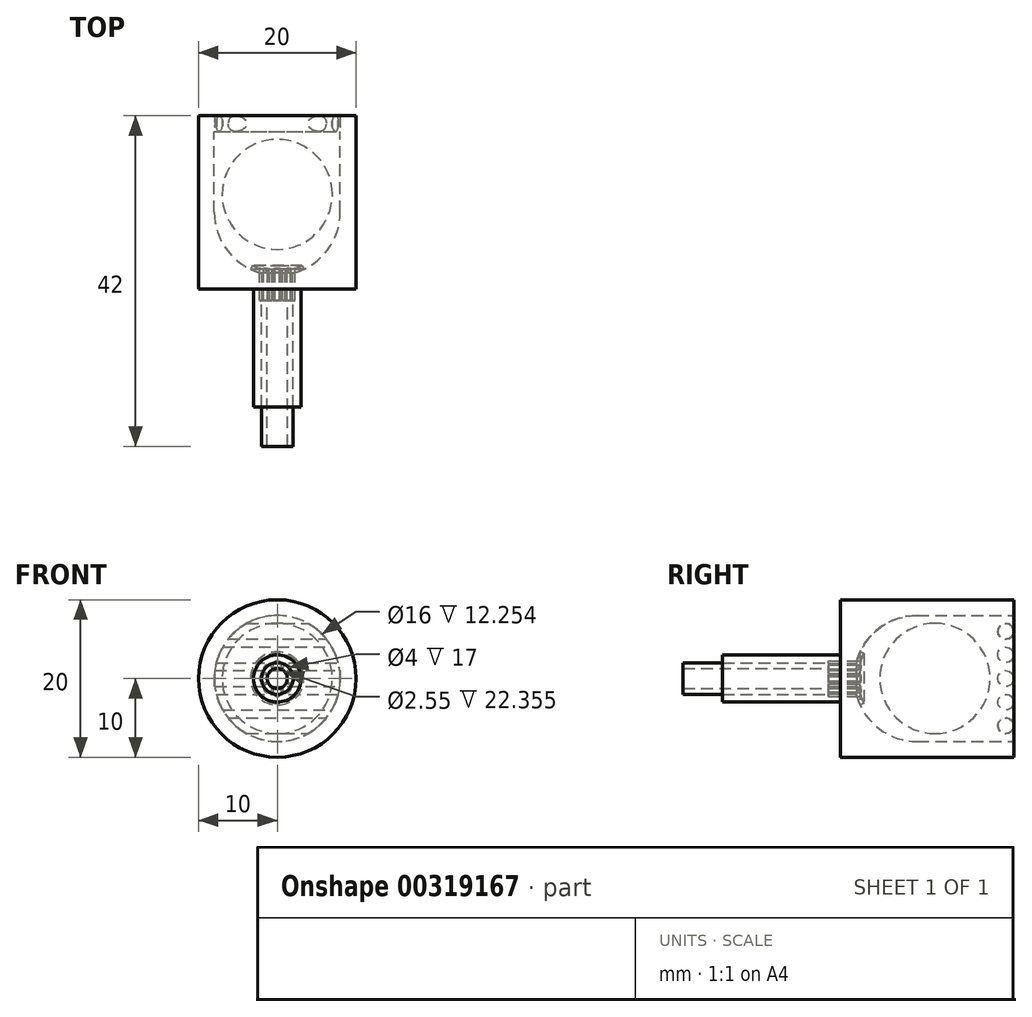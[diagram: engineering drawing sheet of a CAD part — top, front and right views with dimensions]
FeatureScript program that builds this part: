
annotation { "Feature Type Name" : "Feature", "Feature Type Description" : "" }
export const myFeature = defineFeature(function(context is Context, id is Id, definition is map)
    precondition{}
    {
        {
            var Q0;
            Q0=qCreatedBy(makeId("Right.planeOp"),FACE);
            var sketch = newSketch(context, id + "F0", { "sketchPlane" : qUnion([Q0])});
            skLineSegment(sketch, "E0", {"start": v(-37, 3) * mm, "end": v(-22, 3) * mm});
            skLineSegment(sketch, "E1", {"start": v(-22, 3) * mm, "end": v(-22, 2) * mm});
            skLineSegment(sketch, "E2", {"start": v(-22, 2) * mm, "end": v(-37, 2) * mm});
            skLineSegment(sketch, "E3", {"start": v(-37, 2) * mm, "end": v(-37, 3) * mm});
            skLineSegment(sketch, "E4", {"start": v(-22, 3) * mm, "end": v(-22, 10) * mm});
            skLineSegment(sketch, "E5", {"start": v(-22, 10) * mm, "end": v(0, 10) * mm});
            skLineSegment(sketch, "E6", {"start": v(0, 10) * mm, "end": v(0, 8) * mm});
            skLineSegment(sketch, "E7", {"start": v(0, 8) * mm, "end": v(-20, 8) * mm});
            skLineSegment(sketch, "E8", {"start": v(-20, 8) * mm, "end": v(-20, 2) * mm});
            skLineSegment(sketch, "E9", {"start": v(-20, 2) * mm, "end": v(-22, 2) * mm});
            skLineSegment(sketch, "E10", {"start": v(0, 0) * mm, "end": v(-46.36, 0) * mm, "construction": true});
            skCircle(sketch, "E11", {"center": v(-10, 0) * mm, "radius": 7 * mm});
            skCircle(sketch, "E12", {"center": v(-12.25, 0) * mm, "radius": 8 * mm});
            skLineSegment(sketch, "E13", {"start": v(-10, 7) * mm, "end": v(-10, -7) * mm});
            skLineSegment(sketch, "E14", {"start": v(-37, 2) * mm, "end": v(-42, 2) * mm});
            skLineSegment(sketch, "E15", {"start": v(-42, 2) * mm, "end": v(-42, 1.28) * mm});
            skLineSegment(sketch, "E16", {"start": v(-42, 1.28) * mm, "end": v(-18.5, 1.28) * mm});
            skLineSegment(sketch, "E17", {"start": v(-18.5, 1.28) * mm, "end": v(-18.5, 5) * mm});
            skCircle(sketch, "E18", {"center": v(-12.25, 0) * mm, "radius": 7.5 * mm});
            skLineSegment(sketch, "E19", {"start": v(-12.25, 0) * mm, "end": v(-19.5, 3.38) * mm, "construction": true});
            skLineSegment(sketch, "E20", {"start": v(-19.5, 3.38) * mm, "end": v(-19.05, 3.17) * mm});
            skSolve(sketch);
        }
        {
            var Q0;
            Q0=sQuery(id+"F0.wireOp",EDGE,"E17");
            cPlane(context, id + "F1", {"entities" : qUnion([Q0]), "cplaneType" : CPlaneType.LINE_ANGLE, "offset" : 25 * mm, "angle" : 90 * degree, "width" : 150 * mm, "height" : 150 * mm});
        }
        {
            var Q0;
            Q0=qCreatedBy(id+"F1.planeOp",FACE);
            var sketch = newSketch(context, id + "F2", { "sketchPlane" : qUnion([Q0])});
            skLineSegment(sketch, "E21.0", {"start": v(0, 1.28) * mm, "end": v(0, 5) * mm});
            skCircle(sketch, "E22", {"center": v(0, 1.68) * mm, "radius": 0.55 * mm});
            skCircle(sketch, "E23.1.0", {"center": v(-1.2, 1.17) * mm, "radius": 0.55 * mm});
            skCircle(sketch, "E23.2.0", {"center": v(-1.7, -0.03) * mm, "radius": 0.55 * mm});
            skCircle(sketch, "E23.3.0", {"center": v(-1.2, -1.23) * mm, "radius": 0.55 * mm});
            skCircle(sketch, "E23.4.0", {"center": v(0.01, -1.72) * mm, "radius": 0.55 * mm});
            skPoint(sketch, "E23.center", {"position": v(0, -0.02) * mm});
            skCircle(sketch, "E24.1.5.0", {"center": v(1.21, -1.22) * mm, "radius": 0.55 * mm});
            skCircle(sketch, "E24.1.6.0", {"center": v(1.7, -0.02) * mm, "radius": 0.55 * mm});
            skCircle(sketch, "E24.1.7.0", {"center": v(1.2, 1.18) * mm, "radius": 0.55 * mm});
            skSolve(sketch);
        }
        {
            var Q0;
            Q0=sQuery(id+"F0.wireOp",EDGE,"E6");
            cPlane(context, id + "F3", {"entities" : qUnion([Q0]), "cplaneType" : CPlaneType.LINE_ANGLE, "offset" : 25 * mm, "angle" : 0 * degree, "width" : 150 * mm, "height" : 150 * mm});
        }
        {
            var Q0;
            Q0=qCreatedBy(id+"F3.planeOp",FACE);
            var sketch = newSketch(context, id + "F4", { "sketchPlane" : qUnion([Q0])});
            skLineSegment(sketch, "E25.0", {"start": v(22, 10) * mm, "end": v(0, 10) * mm});
            skLineSegment(sketch, "E26.MirrorCS", {"start": v(22, -10) * mm, "end": v(0, -10) * mm});
            skLineSegment(sketch, "E27", {"start": v(1, 10) * mm, "end": v(1, -10) * mm, "construction": true});
            skCircle(sketch, "E28", {"center": v(1, 9) * mm, "radius": 1 * mm});
            skCircle(sketch, "E29.0.1.0", {"center": v(1, 6) * mm, "radius": 1 * mm});
            skCircle(sketch, "E29.0.2.0", {"center": v(1, 3) * mm, "radius": 1 * mm});
            skCircle(sketch, "E29.0.3.0", {"center": v(1, 0) * mm, "radius": 1 * mm});
            skCircle(sketch, "E29.0.4.0", {"center": v(1, -3) * mm, "radius": 1 * mm});
            skCircle(sketch, "E29.0.5.0", {"center": v(1, -6) * mm, "radius": 1 * mm});
            skCircle(sketch, "E29.0.6.0", {"center": v(1, -9) * mm, "radius": 1 * mm});
            skLineSegment(sketch, "E29.direction1", {"start": v(1, 9) * mm, "end": v(26, 9) * mm, "construction": true});
            skLineSegment(sketch, "E29.direction2", {"start": v(1, 9) * mm, "end": v(1, 6) * mm, "construction": true});
            skSolve(sketch);
        }
        {
            var Q0;
            Q0=makeQuery(id+"F0.imprint","IMPRINT",FACE,{"disambiguationData":[TD([[makeQuery(id+"F0.imprint","IMPRINT",EDGE,{"derivedFrom":sQuery(id+"F0.wireOp",EDGE,"E0")}),-1.0]])]});
            var Q1;
            Q1=makeQuery(id+"F0.imprint","IMPRINT",FACE,{"disambiguationData":[TD([[makeQuery(id+"F0.imprint","IMPRINT",EDGE,{"derivedFrom":sQuery(id+"F0.wireOp",EDGE,"E1")}),1.0]])]});
            var Q2;
            {var subQ0=sQuery(id+"F0.wireOp",EDGE,"E8");Q2=makeQuery(id+"F0.imprint","IMPRINT",FACE,{"disambiguationData":[TD([[makeQuery(id+"F0.imprint","IMPRINT",EDGE,{"derivedFrom":subQ0}),1.0]])]});}
            var Q3;
            Q3=sQuery(id+"F0.wireOp",EDGE,"E10");
            revolve(context, id + "F5", {"entities" : qUnion([Q0, Q1, Q2]), "axis" : qUnion([Q3]), "revolveType" : RevolveType.FULL});
        }
        {
            var Q0;
            {var subQ0=sQuery(id+"F0.wireOp",EDGE,"E13");Q0=makeQuery(id+"F0.imprint","IMPRINT",FACE,{"disambiguationData":[TD([[makeQuery(id+"F0.imprint","IMPRINT",EDGE,{"derivedFrom":subQ0}),-1.0]])]});}
            var Q1;
            Q1=sQuery(id+"F0.wireOp",EDGE,"E13");
            revolve(context, id + "F6", {"entities" : qUnion([Q0]), "axis" : qUnion([Q1]), "revolveType" : RevolveType.FULL});
        }
        {
            var Q0;
            {var subQ0=sQuery(id+"F0.wireOp",EDGE,"E20");Q0=makeQuery(id+"F0.imprint","IMPRINT",FACE,{"disambiguationData":[TD([[makeQuery(id+"F0.imprint","IMPRINT",EDGE,{"derivedFrom":subQ0}),-1.0]])]});}
            var Q1;
            Q1=makeQuery(id+"F0.imprint","IMPRINT",FACE,{"disambiguationData":[TD([[makeQuery(id+"F0.imprint","IMPRINT",EDGE,{"derivedFrom":sQuery(id+"F0.wireOp",EDGE,"E2")}),1.0]])]});
            var Q2;
            Q2=sQuery(id+"F0.wireOp",EDGE,"E10");
            revolve(context, id + "F7", {"entities" : qUnion([Q0, Q1]), "axis" : qUnion([Q2]), "revolveType" : RevolveType.FULL});
        }
        {
            var Q0;
            {var subQ0=sQuery(id+"F2.wireOp",EDGE,"E22");var subQ1=sQuery(id+"F2.wireOp",EDGE,"E21.0");var subQ2=makeQuery(id+"F2.imprint","INTERSECT",VERTEX,{"disambiguationData":[OD(0.0)],"derivedFrom":[subQ1,subQ0]});Q0=makeQuery(id+"F2.imprint","IMPRINT",FACE,{"disambiguationData":[TD([[makeQuery(id+"F2.imprint","IMPRINT",EDGE,{"disambiguationData":[TD([[subQ2,-1.0]])],"derivedFrom":subQ1}),1.0]])]});}
            var Q1;
            {var subQ0=sQuery(id+"F2.wireOp",EDGE,"E22");var subQ1=sQuery(id+"F2.wireOp",EDGE,"E21.0");var subQ2=makeQuery(id+"F2.imprint","INTERSECT",VERTEX,{"disambiguationData":[OD(0.0)],"derivedFrom":[subQ1,subQ0]});Q1=makeQuery(id+"F2.imprint","IMPRINT",FACE,{"disambiguationData":[TD([[makeQuery(id+"F2.imprint","IMPRINT",EDGE,{"disambiguationData":[TD([[subQ2,-1.0]])],"derivedFrom":subQ1}),-1.0]])]});}
            var Q2;
            Q2=makeQuery(id+"F2.imprint","IMPRINT",FACE,{"disambiguationData":[TD([[makeQuery(id+"F2.imprint","IMPRINT",EDGE,{"derivedFrom":sQuery(id+"F2.wireOp",EDGE,"E23.11.0")}),1.0]])]});
            var Q3;
            Q3=makeQuery(id+"F2.imprint","IMPRINT",FACE,{"disambiguationData":[TD([[makeQuery(id+"F2.imprint","IMPRINT",EDGE,{"derivedFrom":sQuery(id+"F2.wireOp",EDGE,"E23.10.0")}),1.0]])]});
            var Q4;
            Q4=makeQuery(id+"F2.imprint","IMPRINT",FACE,{"disambiguationData":[TD([[makeQuery(id+"F2.imprint","IMPRINT",EDGE,{"derivedFrom":sQuery(id+"F2.wireOp",EDGE,"E23.1.0")}),1.0]])]});
            var Q5;
            Q5=makeQuery(id+"F2.imprint","IMPRINT",FACE,{"disambiguationData":[TD([[makeQuery(id+"F2.imprint","IMPRINT",EDGE,{"derivedFrom":sQuery(id+"F2.wireOp",EDGE,"E23.2.0")}),1.0]])]});
            var Q6;
            Q6=makeQuery(id+"F2.imprint","IMPRINT",FACE,{"disambiguationData":[TD([[makeQuery(id+"F2.imprint","IMPRINT",EDGE,{"derivedFrom":sQuery(id+"F2.wireOp",EDGE,"E23.3.0")}),1.0]])]});
            var Q7;
            Q7=makeQuery(id+"F2.imprint","IMPRINT",FACE,{"disambiguationData":[TD([[makeQuery(id+"F2.imprint","IMPRINT",EDGE,{"derivedFrom":sQuery(id+"F2.wireOp",EDGE,"E23.4.0")}),1.0]])]});
            var Q8;
            Q8=makeQuery(id+"F2.imprint","IMPRINT",FACE,{"disambiguationData":[TD([[makeQuery(id+"F2.imprint","IMPRINT",EDGE,{"derivedFrom":sQuery(id+"F2.wireOp",EDGE,"E23.5.0")}),1.0]])]});
            var Q9;
            Q9=makeQuery(id+"F2.imprint","IMPRINT",FACE,{"disambiguationData":[TD([[makeQuery(id+"F2.imprint","IMPRINT",EDGE,{"derivedFrom":sQuery(id+"F2.wireOp",EDGE,"E23.6.0")}),1.0]])]});
            var Q10;
            Q10=makeQuery(id+"F2.imprint","IMPRINT",FACE,{"disambiguationData":[TD([[makeQuery(id+"F2.imprint","IMPRINT",EDGE,{"derivedFrom":sQuery(id+"F2.wireOp",EDGE,"E23.7.0")}),1.0]])]});
            var Q11;
            Q11=makeQuery(id+"F2.imprint","IMPRINT",FACE,{"disambiguationData":[TD([[makeQuery(id+"F2.imprint","IMPRINT",EDGE,{"derivedFrom":sQuery(id+"F2.wireOp",EDGE,"E23.8.0")}),1.0]])]});
            var Q12;
            Q12=makeQuery(id+"F2.imprint","IMPRINT",FACE,{"disambiguationData":[TD([[makeQuery(id+"F2.imprint","IMPRINT",EDGE,{"derivedFrom":sQuery(id+"F2.wireOp",EDGE,"E23.9.0")}),1.0]])]});
            var Q13;
            Q13=makeQuery(id+"F2.imprint","IMPRINT",FACE,{"disambiguationData":[TD([[makeQuery(id+"F2.imprint","IMPRINT",EDGE,{"derivedFrom":sQuery(id+"F2.wireOp",EDGE,"E22")}),1.0]])]});
            var Q14;
            Q14=makeQuery(id+"F2.imprint","IMPRINT",FACE,{"disambiguationData":[TD([[makeQuery(id+"F2.imprint","IMPRINT",EDGE,{"derivedFrom":sQuery(id+"F2.wireOp",EDGE,"E24.1.7.0")}),1.0]])]});
            var Q15;
            Q15=makeQuery(id+"F2.imprint","IMPRINT",FACE,{"disambiguationData":[TD([[makeQuery(id+"F2.imprint","IMPRINT",EDGE,{"derivedFrom":sQuery(id+"F2.wireOp",EDGE,"E24.1.6.0")}),1.0]])]});
            var Q16;
            Q16=makeQuery(id+"F2.imprint","IMPRINT",FACE,{"disambiguationData":[TD([[makeQuery(id+"F2.imprint","IMPRINT",EDGE,{"derivedFrom":sQuery(id+"F2.wireOp",EDGE,"E24.1.5.0")}),1.0]])]});
            extrude(context, id + "F8", {"entities" : qUnion([Q0, Q1, Q2, Q3, Q4, Q5, Q6, Q7, Q8, Q9, Q10, Q11, Q12, Q13, Q14, Q15, Q16]), "operationType" : NewBodyOperationType.REMOVE, "oppositeDirection" : true, "depth" : 5 * mm});
        }
        {
            var Q0;
            Q0=makeQuery(id+"F4.imprint","IMPRINT",FACE,{"disambiguationData":[TD([[makeQuery(id+"F4.imprint","IMPRINT",EDGE,{"derivedFrom":sQuery(id+"F4.wireOp",EDGE,"E29.0.6.0")}),1.0]])]});
            var Q1;
            Q1=makeQuery(id+"F4.imprint","IMPRINT",FACE,{"disambiguationData":[TD([[makeQuery(id+"F4.imprint","IMPRINT",EDGE,{"derivedFrom":sQuery(id+"F4.wireOp",EDGE,"E29.0.5.0")}),1.0]])]});
            var Q2;
            Q2=makeQuery(id+"F4.imprint","IMPRINT",FACE,{"disambiguationData":[TD([[makeQuery(id+"F4.imprint","IMPRINT",EDGE,{"derivedFrom":sQuery(id+"F4.wireOp",EDGE,"E29.0.4.0")}),1.0]])]});
            var Q3;
            Q3=makeQuery(id+"F4.imprint","IMPRINT",FACE,{"disambiguationData":[TD([[makeQuery(id+"F4.imprint","IMPRINT",EDGE,{"derivedFrom":sQuery(id+"F4.wireOp",EDGE,"E29.0.3.0")}),1.0]])]});
            var Q4;
            Q4=makeQuery(id+"F4.imprint","IMPRINT",FACE,{"disambiguationData":[TD([[makeQuery(id+"F4.imprint","IMPRINT",EDGE,{"derivedFrom":sQuery(id+"F4.wireOp",EDGE,"E29.0.2.0")}),1.0]])]});
            var Q5;
            Q5=makeQuery(id+"F4.imprint","IMPRINT",FACE,{"disambiguationData":[TD([[makeQuery(id+"F4.imprint","IMPRINT",EDGE,{"derivedFrom":sQuery(id+"F4.wireOp",EDGE,"E29.0.1.0")}),1.0]])]});
            var Q6;
            Q6=makeQuery(id+"F4.imprint","IMPRINT",FACE,{"disambiguationData":[TD([[makeQuery(id+"F4.imprint","IMPRINT",EDGE,{"derivedFrom":sQuery(id+"F4.wireOp",EDGE,"E28")}),1.0]])]});
            extrude(context, id + "F9", {"entities" : qUnion([Q0, Q1, Q2, Q3, Q4, Q5, Q6]), "operationType" : NewBodyOperationType.ADD, "endBound" : BoundingType.UP_TO_NEXT, "depth" : 25 * mm, "hasSecondDirection" : true, "secondDirectionBound" : SecondDirectionBoundingType.UP_TO_NEXT, "secondDirectionOppositeDirection" : true, "secondDirectionDepth" : 25 * mm});
        }
    });
